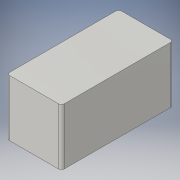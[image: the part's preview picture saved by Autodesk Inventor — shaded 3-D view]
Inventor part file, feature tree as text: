
AUTODESK INVENTOR PART (.ipt)
format: ipt  version: 2021.2 (Build 252289000, 289)  size: 93,184 bytes
history: native  units: mm
features: other x1, extrude x1, fillet x1, sketch x1
ambient origin geometry x8: Origin, YZ Plane, XZ Plane, XY Plane, X Axis, Y Axis, Z Axis, Center Point
bodies: Body1 (feature_tree)
feature tree (4):
  other  "Sólido1"
  extrude  "Extrusión1"  Depth=40.6mm
  fillet  "Empalme1"  Radius=20.5mm
  sketch  "Boceto1"  dims[d0=19.8mm d1=40.6mm d2=20.5mm d3=0.0mm d4=1.0mm]
